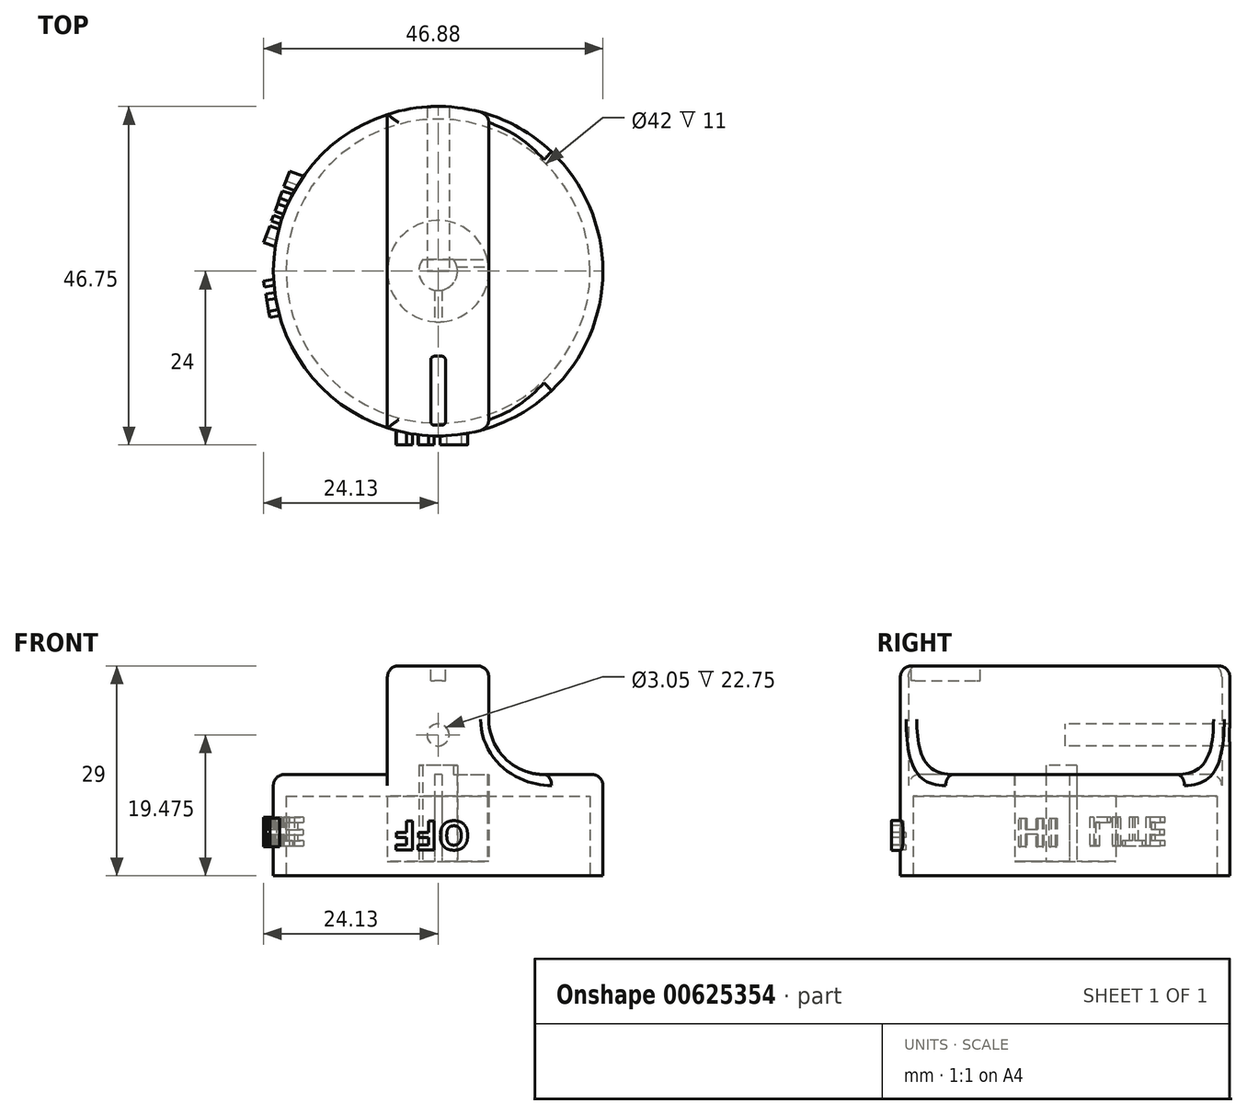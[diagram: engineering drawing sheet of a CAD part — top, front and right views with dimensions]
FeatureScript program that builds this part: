
annotation { "Feature Type Name" : "Feature", "Feature Type Description" : "" }
export const myFeature = defineFeature(function(context is Context, id is Id, definition is map)
    precondition{}
    {
        {
            var Q0;
            Q0=qCreatedBy(makeId("Top.planeOp"),FACE);
            var sketch = newSketch(context, id + "F0", { "sketchPlane" : qUnion([Q0])});
            skCircle(sketch, "E0", {"center": v(0, 0) * mm, "radius": 22.75 * mm});
            skSolve(sketch);
        }
        {
            var Q0;
            Q0=qSketchRegion(id+"F0",true);
            extrude(context, id + "F1", {"entities" : qUnion([Q0]), "depth" : 14 * mm, "offsetDistance" : 25.4 * mm});
        }
        {
            var Q0;
            Q0=makeQuery(id+"F1.opExtrude","CAP_FACE",FACE,{"disambiguationData":[OSD([sQuery(id+"F0.wireOp",EDGE,"E0")])],"isStart":false});
            var sketch = newSketch(context, id + "F2", { "sketchPlane" : qUnion([Q0])});
            skLineSegment(sketch, "E1.left", {"start": v(-7, 21.65) * mm, "end": v(-7, -21.65) * mm});
            skLineSegment(sketch, "E1.right", {"start": v(7, 21.65) * mm, "end": v(7, -21.65) * mm});
            skPoint(sketch, "E2", {"position": v(0, 24.49) * mm});
            skLineSegment(sketch, "E3", {"start": v(0, 34.26) * mm, "end": v(0, -28.44) * mm, "construction": true});
            skLineSegment(sketch, "E4", {"start": v(19.58, 0) * mm, "end": v(-22.13, 0) * mm, "construction": true});
            skArc(sketch, "E5.0", {"start": v(-7, -21.65) * mm, "mid": v(0, -22.75) * mm, "end": v(7, -21.65) * mm});
            skArc(sketch, "E6.trimOffspring", {"start": v(7, 21.65) * mm, "mid": v(0, 22.75) * mm, "end": v(-7, 21.65) * mm});
            skPoint(sketch, "E7.orphan", {"position": v(-7, 24.49) * mm});
            skPoint(sketch, "E1.bottom.end.orphan", {"position": v(7, 24.49) * mm});
            skPoint(sketch, "E8.orphan", {"position": v(7, -23.15) * mm});
            skSolve(sketch);
        }
        {
            var Q0;
            Q0=qSketchRegion(id+"F2",true);
            extrude(context, id + "F3", {"entities" : qUnion([Q0]), "operationType" : NewBodyOperationType.ADD, "depth" : 15 * mm, "offsetDistance" : 25 * mm});
        }
        {
            var Q0;
            Q0=makeQuery(id+"F3.opExtrude","CAP_FACE",FACE,{"disambiguationData":[OSD([sQuery(id+"F2.wireOp",EDGE,"E1.left"),sQuery(id+"F2.wireOp",EDGE,"E1.right"),sQuery(id+"F2.wireOp",EDGE,"E5.0"),sQuery(id+"F2.wireOp",EDGE,"E6.trimOffspring")])],"isStart":false});
            var sketch = newSketch(context, id + "F4", { "sketchPlane" : qUnion([Q0])});
            skLineSegment(sketch, "E9.bottom", {"start": v(0.5, -21.28) * mm, "end": v(-0.5, -21.28) * mm});
            skLineSegment(sketch, "E9.top", {"start": v(0.5, -11.75) * mm, "end": v(-0.5, -11.75) * mm});
            skLineSegment(sketch, "E9.left", {"start": v(1.02, -20.77) * mm, "end": v(1.02, -12.26) * mm});
            skLineSegment(sketch, "E9.right", {"start": v(-1.02, -20.77) * mm, "end": v(-1.02, -12.26) * mm});
            skPoint(sketch, "E10", {"position": v(0, -21.28) * mm});
            skLineSegment(sketch, "E11", {"start": v(0, -16.34) * mm, "end": v(0, 0) * mm, "construction": true});
            skPoint(sketch, "E12.visualSharp", {"position": v(1.02, -21.28) * mm});
            skArc(sketch, "E12.filletArc", {"start": v(0.5, -21.28) * mm, "mid": v(0.87, -21.13) * mm, "end": v(1.02, -20.77) * mm});
            skPoint(sketch, "E13.visualSharp", {"position": v(-1.02, -21.28) * mm});
            skArc(sketch, "E13.filletArc", {"start": v(-1.02, -20.77) * mm, "mid": v(-0.87, -21.13) * mm, "end": v(-0.5, -21.28) * mm});
            skPoint(sketch, "E14.visualSharp", {"position": v(-1.02, -11.75) * mm});
            skArc(sketch, "E14.filletArc", {"start": v(-0.5, -11.75) * mm, "mid": v(-0.87, -11.9) * mm, "end": v(-1.02, -12.26) * mm});
            skPoint(sketch, "E15.visualSharp", {"position": v(1.02, -11.75) * mm});
            skArc(sketch, "E15.filletArc", {"start": v(1.02, -12.26) * mm, "mid": v(0.87, -11.9) * mm, "end": v(0.5, -11.75) * mm});
            skSolve(sketch);
        }
        {
            var Q0;
            Q0=makeQuery(id+"F3.opExtrude","CAP_EDGE",EDGE,{"disambiguationData":[OSD([sQuery(id+"F2.wireOp",EDGE,"E1.left")])],"isStart":true});
            var Q1;
            Q1=makeQuery(id+"F3.opExtrude","CAP_EDGE",EDGE,{"disambiguationData":[OSD([sQuery(id+"F2.wireOp",EDGE,"E1.right")])],"isStart":true});
            fillet(context, id + "F5", {"entities" : qUnion([Q0, Q1]), "radius" : 7.62 * mm, "tangentPropagation" : true, "allowEdgeOverflow" : false});
        }
        {
            var Q0;
            {var subQ0=sQuery(id+"F0.wireOp",EDGE,"E0");Q0=makeQuery(id+"F3.boolean.opBoolean","SPLIT",EDGE,{"disambiguationData":[TD([makeQuery(id+"F3.opExtrude","SWEPT_FACE",FACE,{"disambiguationData":[OSD([sQuery(id+"F2.wireOp",EDGE,"E1.left")])]})])],"derivedFrom":makeQuery(id+"F1.opExtrude","CAP_EDGE",EDGE,{"disambiguationData":[OSD([subQ0])],"isStart":false})});}
            var Q1;
            {var subQ0=sQuery(id+"F0.wireOp",EDGE,"E0");Q1=makeQuery(id+"F3.boolean.opBoolean","SPLIT",EDGE,{"disambiguationData":[TD([makeQuery(id+"F3.opExtrude","SWEPT_FACE",FACE,{"disambiguationData":[OSD([sQuery(id+"F2.wireOp",EDGE,"E1.right")])]})])],"derivedFrom":makeQuery(id+"F1.opExtrude","CAP_EDGE",EDGE,{"disambiguationData":[OSD([subQ0])],"isStart":false})});}
            var Q2;
            Q2=makeQuery(id+"F3.opExtrude","CAP_EDGE",EDGE,{"disambiguationData":[OSD([sQuery(id+"F2.wireOp",EDGE,"E5.0")])],"isStart":false});
            var Q3;
            Q3=makeQuery(id+"F3.opExtrude","CAP_EDGE",EDGE,{"disambiguationData":[OSD([sQuery(id+"F2.wireOp",EDGE,"E1.left")])],"isStart":false});
            var Q4;
            Q4=makeQuery(id+"F3.opExtrude","CAP_EDGE",EDGE,{"disambiguationData":[OSD([sQuery(id+"F2.wireOp",EDGE,"E1.right")])],"isStart":false});
            var Q5;
            Q5=makeQuery(id+"F3.opExtrude","CAP_EDGE",EDGE,{"disambiguationData":[OSD([sQuery(id+"F2.wireOp",EDGE,"E6.trimOffspring")])],"isStart":false});
            fillet(context, id + "F6", {"entities" : qUnion([Q0, Q1, Q2, Q3, Q4, Q5]), "radius" : 1.52 * mm, "tangentPropagation" : true, "allowEdgeOverflow" : false});
        }
        {
            var Q0;
            Q0=makeQuery(id+"F1.opExtrude","CAP_FACE",FACE,{"disambiguationData":[OSD([sQuery(id+"F0.wireOp",EDGE,"E0")])],"isStart":true});
            var sketch = newSketch(context, id + "F7", { "sketchPlane" : qUnion([Q0])});
            skLineSegment(sketch, "E16", {"start": v(0, 0) * mm, "end": v(0, -1.6) * mm});
            skLineSegment(sketch, "E17", {"start": v(0, -1.6) * mm, "end": v(-2.13, -1.6) * mm});
            skCircle(sketch, "E18", {"center": v(0, 0) * mm, "radius": 2.67 * mm});
            skLineSegment(sketch, "E19", {"start": v(-2.13, -1.6) * mm, "end": v(2.13, -1.6) * mm});
            skSolve(sketch);
        }
        {
            var Q0;
            {var subQ0=sQuery(id+"F7.wireOp",EDGE,"E19");var subQ4=makeQuery(id+"F7.imprint","IMPRINT",VERTEX,{"derivedFrom":subQ0});Q0=makeQuery(id+"F7.imprint","IMPRINT",FACE,{"disambiguationData":[TD([[makeQuery(id+"F7.imprint","IMPRINT",EDGE,{"disambiguationData":[TD([[subQ4,1.0]])],"derivedFrom":subQ0}),1.0]])]});}
            extrude(context, id + "F8", {"entities" : qUnion([Q0]), "operationType" : NewBodyOperationType.REMOVE, "oppositeDirection" : true, "depth" : 15.24 * mm, "offsetDistance" : 25.4 * mm});
        }
        {
            var Q0;
            Q0=qSketchRegion(id+"F4",true);
            extrude(context, id + "F9", {"entities" : qUnion([Q0]), "operationType" : NewBodyOperationType.REMOVE, "oppositeDirection" : true, "depth" : 2.03 * mm});
        }
        {
            var Q0;
            Q0=qCreatedBy(makeId("Front.planeOp"),FACE);
            var sketch = newSketch(context, id + "F10", { "sketchPlane" : qUnion([Q0])});
            skCircle(sketch, "E20", {"center": v(0, 19.47) * mm, "radius": 1.52 * mm});
            skSolve(sketch);
        }
        {
            var Q0;
            Q0=qSketchRegion(id+"F10",true);
            extrude(context, id + "F11", {"entities" : qUnion([Q0]), "operationType" : NewBodyOperationType.REMOVE, "endBound" : BoundingType.THROUGH_ALL, "oppositeDirection" : true, "depth" : 25.4 * mm});
        }
        {
            var Q0;
            Q0=makeQuery(id+"F1.opExtrude","CAP_FACE",FACE,{"disambiguationData":[OSD([sQuery(id+"F0.wireOp",EDGE,"E0")])],"isStart":true});
            var sketch = newSketch(context, id + "F12", { "sketchPlane" : qUnion([Q0])});
            skCircle(sketch, "E21", {"center": v(0, 0) * mm, "radius": 7.94 * mm});
            skSolve(sketch);
        }
        {
            var Q0;
            Q0=qSketchRegion(id+"F12",true);
            extrude(context, id + "F13", {"entities" : qUnion([Q0]), "operationType" : NewBodyOperationType.REMOVE, "oppositeDirection" : true, "depth" : 2 * mm, "offsetDistance" : 25 * mm});
        }
        {
            var Q0;
            Q0=makeQuery(id+"F1.opExtrude","CAP_FACE",FACE,{"disambiguationData":[OSD([sQuery(id+"F0.wireOp",EDGE,"E0")])],"isStart":true});
            var sketch = newSketch(context, id + "F14", { "sketchPlane" : qUnion([Q0])});
            skCircle(sketch, "E22", {"center": v(0, 0) * mm, "radius": 21 * mm});
            skCircle(sketch, "E23", {"center": v(0, 0) * mm, "radius": 7 * mm});
            skSolve(sketch);
        }
        {
            var Q0;
            Q0 = qSketchRegion(id + "F14", true);
            extrude(context, id + "F15", {"entities" : qUnion([Q0]), "operationType" : NewBodyOperationType.REMOVE, "oppositeDirection" : true, "depth" : 11 * mm, "offsetDistance" : 25 * mm});
        }
        {
            var Q0;
            Q0=makeQuery(id+"F13.boolean.opBoolean","COPY",FACE,{"derivedFrom":makeQuery(id+"F13.opExtrude","CAP_FACE",FACE,{"disambiguationData":[OSD([sQuery(id+"F12.wireOp",EDGE,"E21")])],"isStart":false})});
            var sketch = newSketch(context, id + "F16", { "sketchPlane" : qUnion([Q0])});
            skLineSegment(sketch, "E24", {"start": v(-2.13, -1.6) * mm, "end": v(-6.81, -1.6) * mm});
            skLineSegment(sketch, "E25", {"start": v(-6.81, -1.6) * mm, "end": v(6.81, -1.6) * mm});
            skLineSegment(sketch, "E26", {"start": v(0, -1.6) * mm, "end": v(0, -0.6) * mm});
            skPoint(sketch, "E26.endSnap0", {"position": v(0, -1.6) * mm});
            skLineSegment(sketch, "E27", {"start": v(0, -0.6) * mm, "end": v(6.97, -0.6) * mm});
            skLineSegment(sketch, "E28", {"start": v(6.97, -0.6) * mm, "end": v(-6.97, -0.6) * mm});
            skLineSegment(sketch, "E29", {"start": v(0, -0.6) * mm, "end": v(0.5, -0.6) * mm});
            skLineSegment(sketch, "E30", {"start": v(0.5, -0.6) * mm, "end": v(0.5, 6.98) * mm});
            skLineSegment(sketch, "E31", {"start": v(0, -0.6) * mm, "end": v(-0.5, -0.6) * mm});
            skLineSegment(sketch, "E32", {"start": v(-0.5, -0.6) * mm, "end": v(-0.5, 6.98) * mm});
            skSolve(sketch);
        }
        {
            var Q0;
            {var subQ0=sQuery(id+"F16.wireOp",EDGE,"E30");var subQ1=makeQuery(id+"F13.opExtrude","CAP_FACE",FACE,{"disambiguationData":[OSD([sQuery(id+"F12.wireOp",EDGE,"E21")])],"isStart":false});var subQ2=makeQuery(id+"F15.boolean.opBoolean","INTERSECT",EDGE,{"derivedFrom":[makeQuery(id+"F13.boolean.opBoolean","COPY",FACE,{"derivedFrom":subQ1}),makeQuery(id+"F15.opExtrude","SWEPT_FACE",FACE,{"disambiguationData":[OSD([sQuery(id+"F14.wireOp",EDGE,"E23")])]})]});var subQ3=makeQuery(id+"F16.imprint","INTERSECT",VERTEX,{"derivedFrom":[subQ2,subQ0]});Q0=makeQuery(id+"F16.imprint","IMPRINT",FACE,{"disambiguationData":[TD([[makeQuery(id+"F16.imprint","IMPRINT",EDGE,{"disambiguationData":[TD([[subQ3,1.0]])],"derivedFrom":subQ0}),1.0]])]});}
            var Q1;
            {var subQ0=sQuery(id+"F16.wireOp",EDGE,"E25");var subQ1=makeQuery(id+"F13.opExtrude","CAP_FACE",FACE,{"disambiguationData":[OSD([sQuery(id+"F12.wireOp",EDGE,"E21")])],"isStart":false});var subQ4=makeQuery(id+"F15.boolean.opBoolean","INTERSECT",EDGE,{"derivedFrom":[makeQuery(id+"F13.boolean.opBoolean","COPY",FACE,{"derivedFrom":subQ1}),makeQuery(id+"F15.opExtrude","SWEPT_FACE",FACE,{"disambiguationData":[OSD([sQuery(id+"F14.wireOp",EDGE,"E23")])]})]});var subQ5=makeQuery(id+"F16.imprint","INTERSECT",VERTEX,{"disambiguationData":[OD(0.0)],"derivedFrom":[subQ4,subQ0]});Q1=makeQuery(id+"F16.imprint","IMPRINT",FACE,{"disambiguationData":[TD([[makeQuery(id+"F16.imprint","IMPRINT",EDGE,{"disambiguationData":[TD([[subQ5,-1.0]])],"derivedFrom":subQ0}),1.0]])]});}
            var Q2;
            {var subQ0=sQuery(id+"F16.wireOp",EDGE,"E25");var subQ1=makeQuery(id+"F13.opExtrude","CAP_FACE",FACE,{"disambiguationData":[OSD([sQuery(id+"F12.wireOp",EDGE,"E21")])],"isStart":false});var subQ4=makeQuery(id+"F15.boolean.opBoolean","INTERSECT",EDGE,{"derivedFrom":[makeQuery(id+"F13.boolean.opBoolean","COPY",FACE,{"derivedFrom":subQ1}),makeQuery(id+"F15.opExtrude","SWEPT_FACE",FACE,{"disambiguationData":[OSD([sQuery(id+"F14.wireOp",EDGE,"E23")])]})]});var subQ5=makeQuery(id+"F16.imprint","INTERSECT",VERTEX,{"disambiguationData":[OD(1.0)],"derivedFrom":[subQ4,subQ0]});Q2=makeQuery(id+"F16.imprint","IMPRINT",FACE,{"disambiguationData":[TD([[makeQuery(id+"F16.imprint","IMPRINT",EDGE,{"disambiguationData":[TD([[subQ5,1.0]])],"derivedFrom":subQ0}),1.0]])]});}
            extrude(context, id + "F17", {"entities" : qUnion([Q0, Q1, Q2]), "operationType" : NewBodyOperationType.REMOVE, "oppositeDirection" : true, "depth" : 12 * mm, "offsetDistance" : 25 * mm});
        }
        {
            var Q0;
            Q0=qCreatedBy(makeId("Front.planeOp"),FACE);
            cPlane(context, id + "F18", {"entities" : qUnion([Q0]), "cplaneType" : CPlaneType.OFFSET, "offset" : 25 * mm, "width" : 150 * mm, "height" : 150 * mm});
        }
        {
            var Q0;
            Q0=qCreatedBy(id+"F18.planeOp",FACE);
            var sketch = newSketch(context, id + "F19", { "sketchPlane" : qUnion([Q0])});
            skText(sketch, "E33", { "text": "OFF", "fontName": "OpenSans-Bold.ttf"});
            const initialGuessF19  = {"E33": [0.0044, 0.00757, -1, 0, 0.004]};
            skSetInitialGuess(sketch, initialGuessF19);
            skSolve(sketch);
        }
        {
            var Q0;
            Q0 = qSketchRegion(id + "F19", true);
            extrude(context, id + "F20", {"entities" : qUnion([Q0]), "operationType" : NewBodyOperationType.ADD, "endBound" : BoundingType.UP_TO_NEXT, "oppositeDirection" : true, "depth" : 2 * mm, "offsetDistance" : 25 * mm, "hasSecondDirection" : true, "secondDirectionOppositeDirection" : true, "secondDirectionDepth" : 1 * mm});
        }
        {
            var Q0;
            Q0=qCreatedBy(makeId("Front.planeOp"),FACE);
            var sketch = newSketch(context, id + "F21", { "sketchPlane" : qUnion([Q0])});
            skLineSegment(sketch, "E34", {"start": v(0, 0) * mm, "end": v(0, 49.56) * mm});
            skSolve(sketch);
        }
        {
            var Q0;
            Q0=sQuery(id+"F21.wireOp",EDGE,"E34");
            cPlane(context, id + "F22", {"entities" : qUnion([Q0]), "cplaneType" : CPlaneType.LINE_ANGLE, "offset" : 25 * mm, "angle" : 160 * degree, "width" : 150 * mm, "height" : 150 * mm});
        }
        {
            var Q0;
            Q0=qCreatedBy(id+"F22.planeOp",FACE);
            var sketch = newSketch(context, id + "F23", { "sketchPlane" : qUnion([Q0])});
            skText(sketch, "E35", { "text": "LITE\n", "fontName": "OpenSans-Bold.ttf"});
            const initialGuessF23  = {"E35": [0.005, 0.0081, -1, 0, 0.004]};
            skSetInitialGuess(sketch, initialGuessF23);
            skSolve(sketch);
        }
        {
            var Q0;
            Q0 = qSketchRegion(id + "F23", true);
            extrude(context, id + "F24", {"entities" : qUnion([Q0]), "operationType" : NewBodyOperationType.ADD, "depth" : 24 * mm, "offsetDistance" : 25 * mm, "hasSecondDirection" : true, "secondDirectionOppositeDirection" : false, "secondDirectionDepth" : 21 * mm});
        }
        {
            var Q0;
            Q0=sQuery(id+"F21.wireOp",EDGE,"E34");
            cPlane(context, id + "F25", {"entities" : qUnion([Q0]), "cplaneType" : CPlaneType.LINE_ANGLE, "offset" : 25 * mm, "angle" : 10 * degree, "width" : 150 * mm, "height" : 150 * mm});
        }
        {
            var Q0;
            Q0=qCreatedBy(id+"F25.planeOp",FACE);
            var sketch = newSketch(context, id + "F26", { "sketchPlane" : qUnion([Q0])});
            skText(sketch, "E36", { "text": "HI\n", "fontName": "OpenSans-Bold.ttf"});
            const initialGuessF26  = {"E36": [-0.00273, 0.004, 1, 0, 0.004]};
            skSetInitialGuess(sketch, initialGuessF26);
            skSolve(sketch);
        }
        {
            var Q0;
            Q0 = qSketchRegion(id + "F26", true);
            extrude(context, id + "F27", {"entities" : qUnion([Q0]), "operationType" : NewBodyOperationType.ADD, "oppositeDirection" : true, "depth" : 24 * mm, "offsetDistance" : 25 * mm, "hasSecondDirection" : true, "secondDirectionOppositeDirection" : true, "secondDirectionDepth" : 21 * mm});
        }
    });
